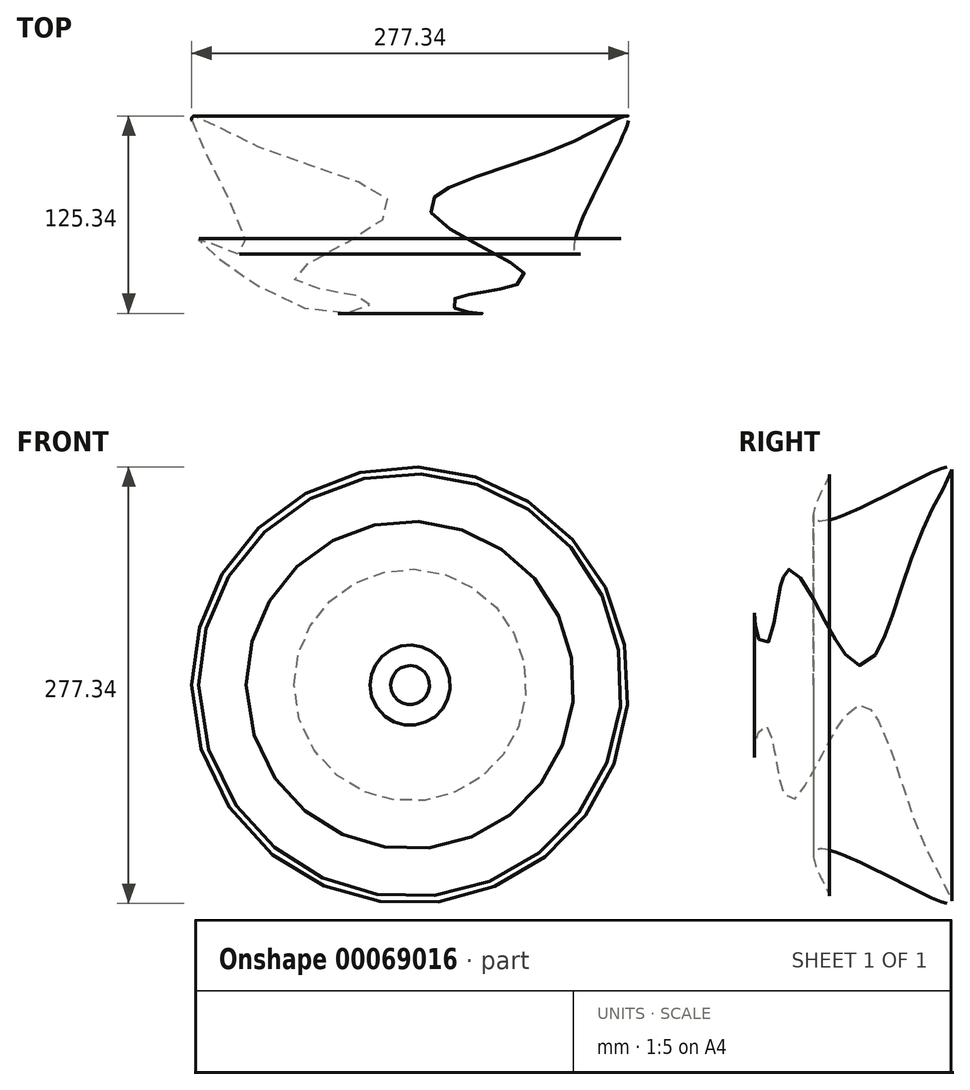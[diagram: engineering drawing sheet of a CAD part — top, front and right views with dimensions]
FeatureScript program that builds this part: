
annotation { "Feature Type Name" : "Feature", "Feature Type Description" : "" }
export const myFeature = defineFeature(function(context is Context, id is Id, definition is map)
    precondition{}
    {
        {
            var Q0;
            Q0=qCreatedBy(makeId("Top.planeOp"),FACE);
            var sketch = newSketch(context, id + "F0", { "sketchPlane" : qUnion([Q0])});
            skFitSpline(sketch, "E0", {"points": [v(-62.27, 68.99) * mm, v(-28.9, -14.86) * mm, v(-57.59, -5.7) * mm, v(15.87, -51.69) * mm, v(49.86, -44.97) * mm, v(2.65, -30.93) * mm, v(63.29, 11.6) * mm, v(-23.6, 53.93) * mm, v(-62.27, 68.99) * mm]});
            skLineSegment(sketch, "E1", {"start": v(76.31, 76.31) * mm, "end": v(76.31, -75.1) * mm});
            skSolve(sketch);
        }
        {
            var Q0;
            Q0=makeQuery(id+"F0.imprint","IMPRINT",FACE,{"disambiguationData":[TD([[makeQuery(id+"F0.imprint","IMPRINT",EDGE,{"derivedFrom":sQuery(id+"F0.wireOp",EDGE,"E0")}),1.0]])]});
            var Q1;
            Q1=sQuery(id+"F0.wireOp",EDGE,"E1");
            revolve(context, id + "F1", {"entities" : qUnion([Q0]), "axis" : qUnion([Q1]), "revolveType" : RevolveType.FULL});
        }
    });
